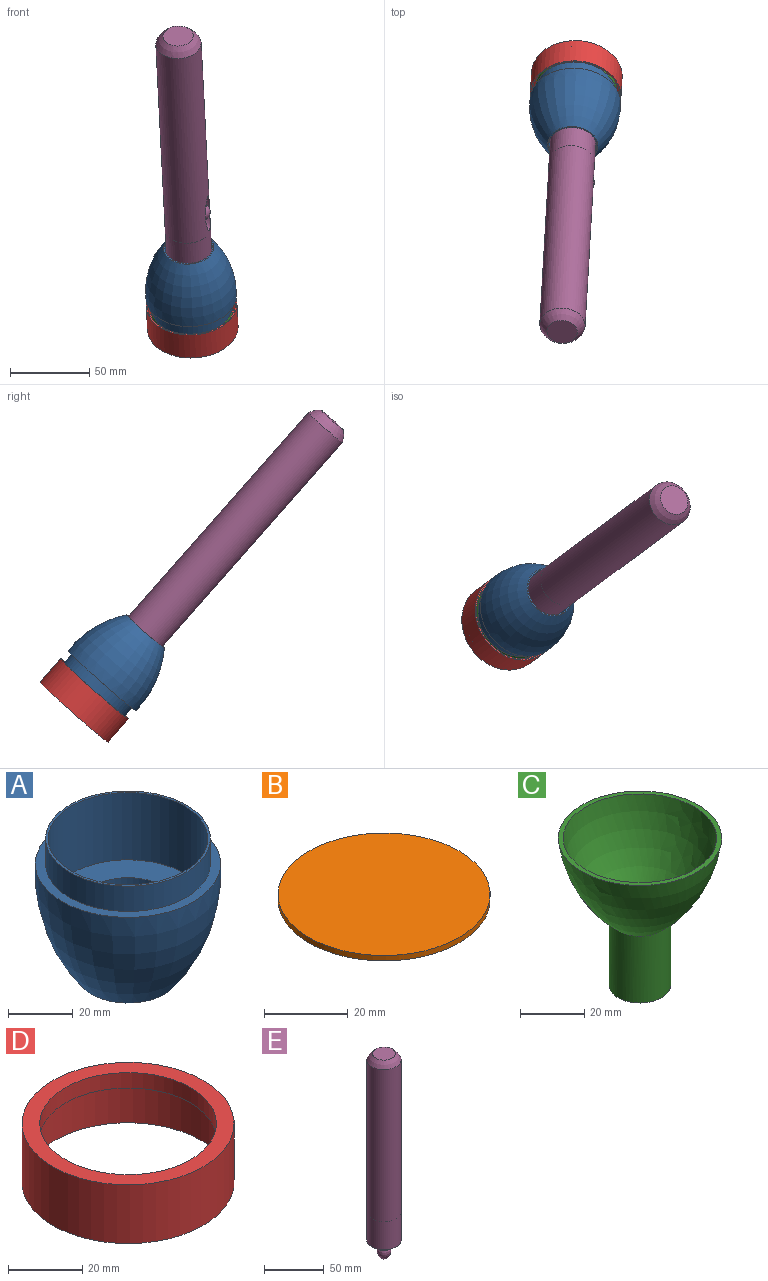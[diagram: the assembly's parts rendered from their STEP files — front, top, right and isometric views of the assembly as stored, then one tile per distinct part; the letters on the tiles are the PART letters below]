
ASSEMBLY  parts=5 mates=4
PART A: 8 faces, bbox 57.3x57.3x50.8 mm
  f0: cylinder r=15.08mm len=30.16mm, axis (0,0,-1), area 2406.9mm2, adj f1,f7
  f1: plane 31.75x31.75mm, normal (0,0,-1), area 77.2mm2, adj f0,f2
  f2: revolved ~57.3x57.3mm, area 6819.3mm2, adj f1,f3
  f3: plane 57.15x57.15mm, normal (0,0,1), area 538.4mm2, adj f2,f4
  f4: cylinder r=25.4mm len=50.8mm, axis (0,0,-1), area 1520.1mm2, adj f3,f5
  f5: plane 50.8x50.8mm, normal (0,0,1), area 124.7mm2, adj f4,f6
  f6: cylinder r=24.61mm len=49.21mm, axis (0,0,1), area 3927mm2, adj f5,f7
  f7: plane 49.21x49.21mm, normal (0,0,1), area 1187.6mm2, adj f0,f6
PART B: 3 faces, bbox 50.8x50.8x1.6 mm
  f0: cylinder r=25.4mm len=50.8mm, axis (0,0,-1), area 253.4mm2, adj f1,f2
  f1: plane 50.8x50.8mm, normal (0,0,1), area 2026.8mm2, adj f0
  f2: plane 50.8x50.8mm, normal (0,0,-1), area 2026.8mm2, adj f0
PART C: 6 faces, bbox 50.8x50.8x55.9 mm
  f0: cylinder r=9.53mm len=25.4mm, axis (0,0,-1), area 1520.1mm2, adj f1,f3
  f1: plane 19.05x19.05mm, normal (0,0,-1), area 87.1mm2, adj f0,f2
  f2: cylinder r=7.94mm len=25.4mm, axis (0,0,-1), area 1266.8mm2, adj f1,f5
  f3: revolved ~50.8x50.8mm, area 4235.8mm2, adj f0,f4
  f4: plane 50.8x50.8mm, normal (0,0,1), area 245.4mm2, adj f3,f5
  f5: revolved ~47.63x47.63mm, area 7772.2mm2, adj f2,f4
PART D: 6 faces, bbox 57.2x57.2x19.4 mm
  f0: cylinder r=27.78mm len=55.56mm, axis (0,0,-1), area 2494mm2, adj f2,f5
  f1: cylinder r=28.57mm len=57.15mm, axis (0,0,-1), area 3477.3mm2, adj f2,f4
  f2: plane 57.15x57.15mm, normal (0,0,-1), area 140.5mm2, adj f0,f1
  f3: cylinder r=23.81mm len=47.63mm, axis (0,0,-1), area 760.1mm2, adj f4,f5
  f4: plane 57.15x57.15mm, normal (0,0,1), area 783.8mm2, adj f1,f3
  f5: plane 55.56x55.56mm, normal (0,0,-1), area 643.3mm2, adj f0,f3
PART E: 14 faces, bbox 28.6x29.4x209.6 mm
  f0: revolved ~28.58x9.53mm, area 319mm2, adj f1,f12,f13
  f1: cylinder r=14.29mm len=184.15mm, axis (0,0,-1), area 16316.8mm2, adj f0,f2,f11
  f2: plane 28.58x28.58mm, normal (0,0,-1), area 35.1mm2, adj f1,f4
  f3: cylinder r=7.94mm len=22.23mm, axis (0,0,-1), area 1108.4mm2, adj f5,f6
  f4: cylinder r=13.89mm len=28.58mm, axis (0,0,-1), area 2494mm2, adj f2,f5
  f5: plane 27.78x27.78mm, normal (0,0,-1), area 408.2mm2, adj f3,f4
  f6: plane 15.88x15.88mm, normal (0,0,-1), area 71.3mm2, adj f3,f7
  f7: cylinder r=6.35mm len=12.7mm, axis (0,0,1), area 506.7mm2, adj f6,f8
  f8: plane 12.7x12.7mm, normal (0,0,-1), area 70.9mm2, adj f7,f9
  f9: revolved ~12.7x11.33mm, area 404.4mm2, adj f8
  f10: plane 19.05x19.05mm, normal (0,0,1), area 285mm2, adj f11
  f11: revolved ~28.58x28.58mm, area 611.5mm2, adj f1,f10
  f12: sphere r=5.58mm, area 83.3mm2, adj f0,f13
  f13: plane 9.15x8.99mm, normal (0,-1,0), area 65.5mm2, adj f0,f12
PLACE A rot(axis=(-0.58,0.77,0.28),153.6deg) t=(213.14,148.67,266.74)mm
PLACE B rot(axis=(0.28,0.33,-0.9),111.7deg) t=(215.48,189.62,220.34)mm
PLACE C rot(axis=(-0.99,0.14,0.03),138.7deg) t=(213.11,148.25,267.22)mm
PLACE D rot(axis=(-0.99,0.14,0.03),138.7deg) t=(214.96,180.62,230.54)mm
PLACE E rot(axis=(0.28,0.33,-0.9),111.7deg) t=(213.62,157.07,257.23)mm
MATE cylindrical D.f0 <-> A.f4  axis (-0.04,-0.66,0.75) through (214.96,180.62,230.54)mm
MATE slider B.f0 <-> C.f2  axis (-0.04,-0.66,0.75) through (215.42,188.57,221.53)mm
MATE slider E.f1 <-> A.f4  axis (0.04,0.66,-0.75) through (210.13,96.19,326.22)mm
MATE slider C.f0 <-> E.f4  axis (-0.04,-0.66,0.75) through (213.11,148.25,267.22)mm
